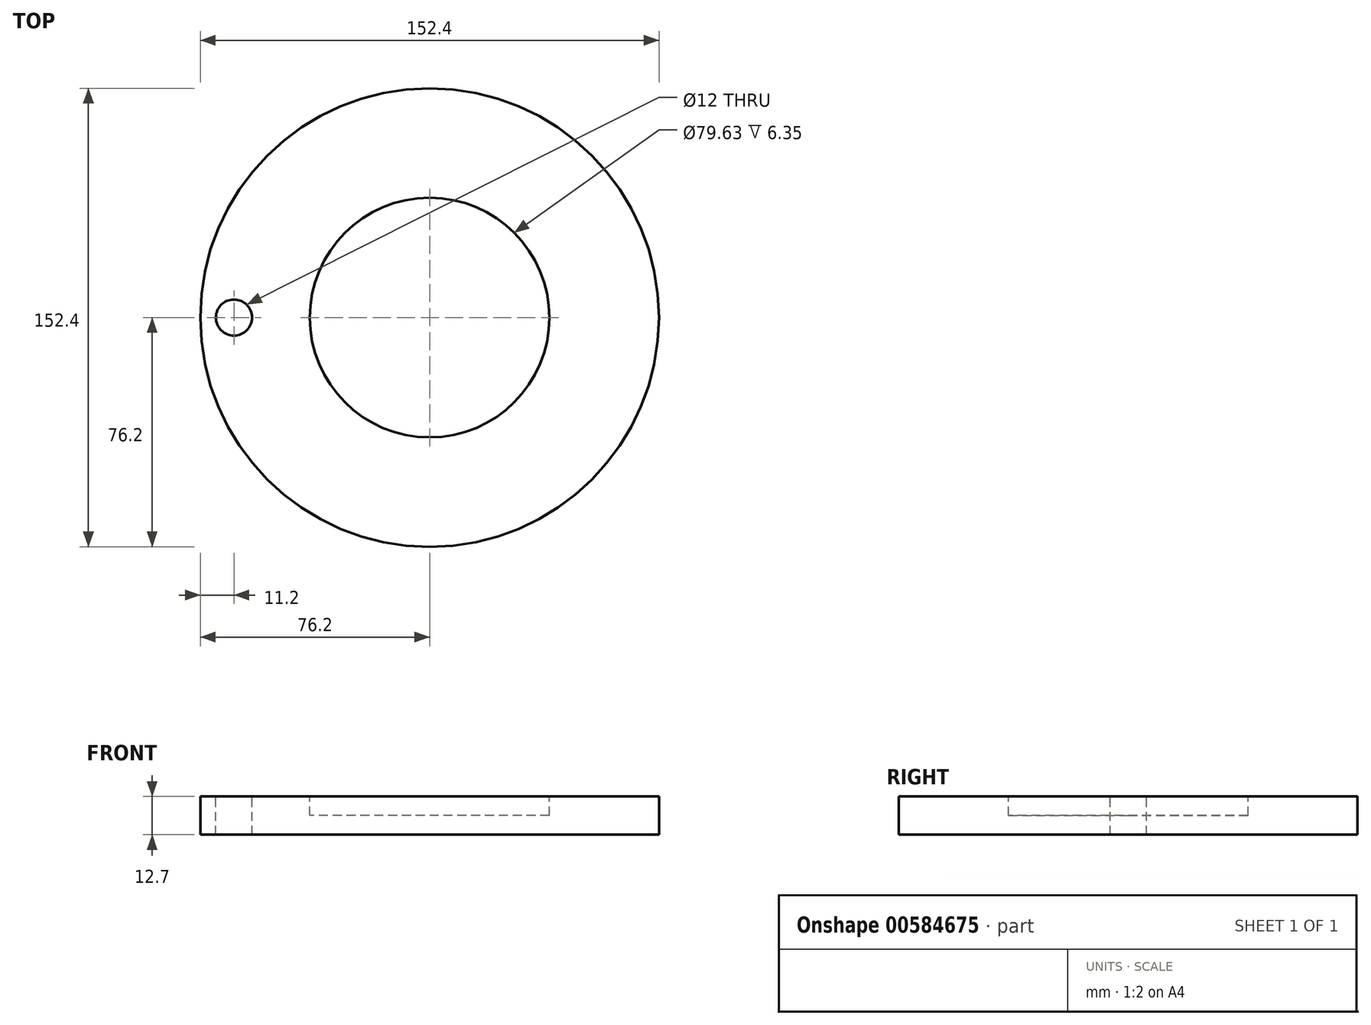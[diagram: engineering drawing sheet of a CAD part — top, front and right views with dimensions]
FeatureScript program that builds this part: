
annotation { "Feature Type Name" : "Feature", "Feature Type Description" : "" }
export const myFeature = defineFeature(function(context is Context, id is Id, definition is map)
    precondition{}
    {
        {
            var Q0;
            Q0=qCreatedBy(makeId("Top.planeOp"),FACE);
            var sketch = newSketch(context, id + "F0", { "sketchPlane" : qUnion([Q0])});
            skCircle(sketch, "E0", {"center": v(0, 0) * mm, "radius": 76.2 * mm});
            skSolve(sketch);
        }
        {
            var Q0;
            Q0=makeQuery(id+"F0.imprint","IMPRINT",FACE,{"disambiguationData":[TD([[makeQuery(id+"F0.imprint","IMPRINT",EDGE,{"derivedFrom":sQuery(id+"F0.wireOp",EDGE,"E0")}),1.0]])]});
            extrude(context, id + "F1", {"entities" : qUnion([Q0]), "depth" : 12.7 * mm, "offsetDistance" : 25 * mm});
        }
        {
            var Q0;
            Q0=makeQuery(id+"F1.opExtrude","CAP_FACE",FACE,{"disambiguationData":[OSD([sQuery(id+"F0.wireOp",EDGE,"E0")])],"isStart":false});
            var sketch = newSketch(context, id + "F2", { "sketchPlane" : qUnion([Q0])});
            skPoint(sketch, "E1", {"position": v(-65, 0) * mm});
            skSolve(sketch);
        }
        {
            var Q0;
            Q0=sQuery(id+"F2.wireOp",VERTEX,"E1");
            var Q1;
            Q1=makeQuery(id+"F1.opExtrude","SWEPT_BODY",BODY,{"disambiguationData":[OSD([sQuery(id+"F0.wireOp",EDGE,"E0")])]});
            hole(context, id + "F3", {"style" : HoleStyle.SIMPLE, "endStyle" : HoleEndStyle.THROUGH, "holeDiameter" : 12 * mm, "majorDiameter" : 5 * mm, "isTappedThrough" : true, "tappedDepth" : 12 * mm, "tapClearance" : 3, "locations" : qUnion([Q0]), "scope" : qUnion([Q1])});
        }
        {
            var Q0;
            Q0=makeQuery(id+"F1.opExtrude","CAP_FACE",FACE,{"disambiguationData":[OSD([sQuery(id+"F0.wireOp",EDGE,"E0")])],"isStart":false});
            var sketch = newSketch(context, id + "F4", { "sketchPlane" : qUnion([Q0])});
            skCircle(sketch, "E2", {"center": v(0, 0) * mm, "radius": 39.81 * mm});
            skSolve(sketch);
        }
        {
            var Q0;
            Q0=makeQuery(id+"F4.imprint","IMPRINT",FACE,{"disambiguationData":[TD([[makeQuery(id+"F4.imprint","IMPRINT",EDGE,{"derivedFrom":sQuery(id+"F4.wireOp",EDGE,"E2")}),1.0]])]});
            extrude(context, id + "F5", {"entities" : qUnion([Q0]), "operationType" : NewBodyOperationType.REMOVE, "oppositeDirection" : true, "depth" : 6.35 * mm, "offsetDistance" : 25 * mm});
        }
    });
